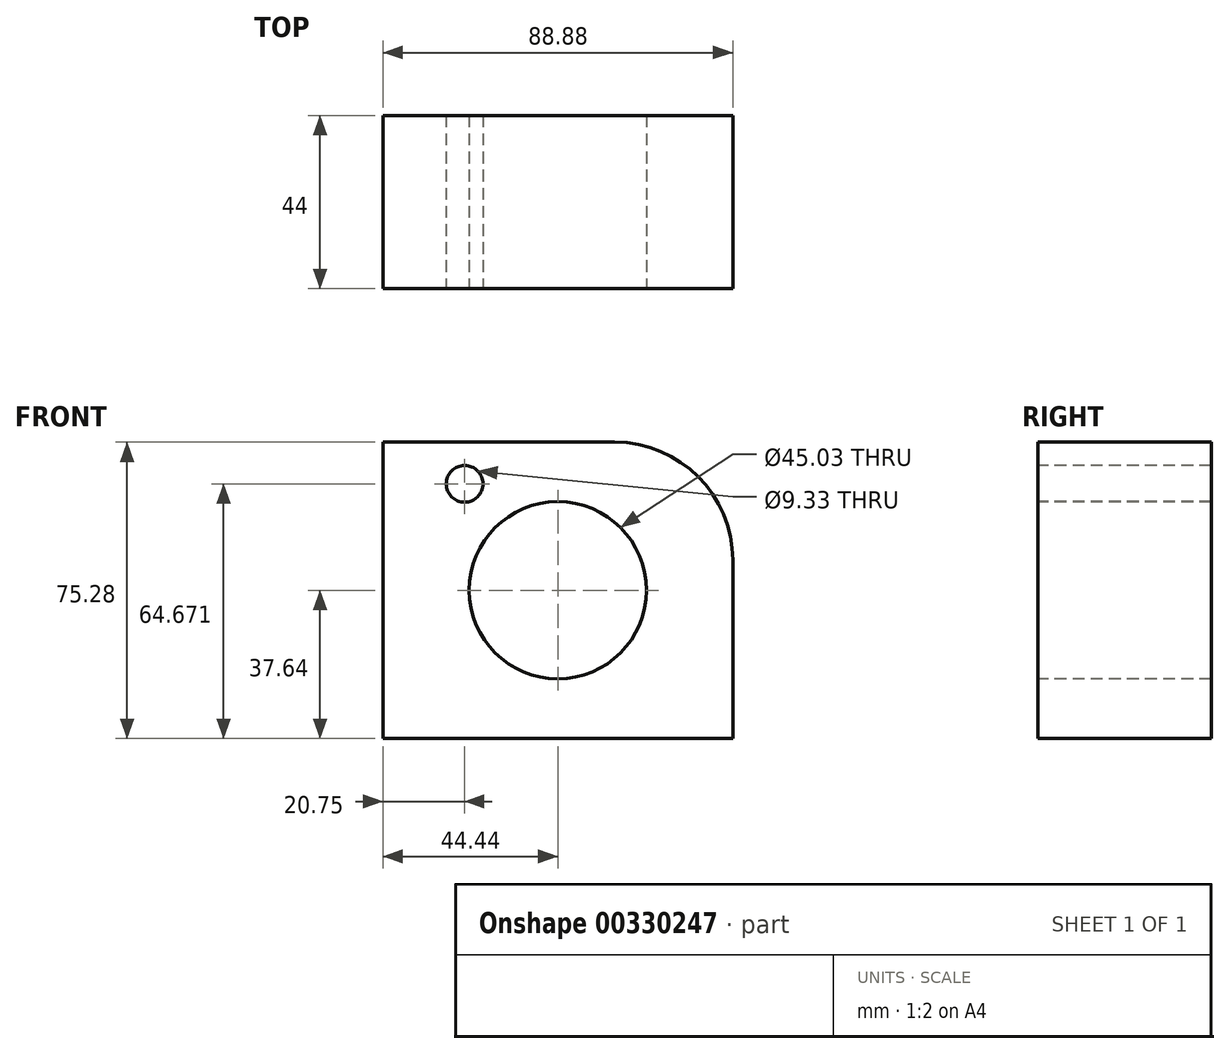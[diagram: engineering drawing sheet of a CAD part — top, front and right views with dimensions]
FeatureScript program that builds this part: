
annotation { "Feature Type Name" : "Feature", "Feature Type Description" : "" }
export const myFeature = defineFeature(function(context is Context, id is Id, definition is map)
    precondition{}
    {
        {
            var Q0;
            Q0=qCreatedBy(makeId("Front.planeOp"),FACE);
            var sketch = newSketch(context, id + "F0", { "sketchPlane" : qUnion([Q0])});
            skLineSegment(sketch, "E0.bottom", {"start": v(-44.44, 37.64) * mm, "end": v(44.44, 37.64) * mm});
            skLineSegment(sketch, "E0.top", {"start": v(-44.44, -37.64) * mm, "end": v(44.44, -37.64) * mm});
            skLineSegment(sketch, "E0.left", {"start": v(-44.44, 37.64) * mm, "end": v(-44.44, -37.64) * mm});
            skLineSegment(sketch, "E0.right", {"start": v(44.44, 37.64) * mm, "end": v(44.44, -37.64) * mm});
            skPoint(sketch, "E0.middle", {"position": v(0, 0) * mm});
            skSolve(sketch);
        }
        {
            var Q0;
            Q0=makeQuery(id+"F0.imprint","IMPRINT",FACE,{"disambiguationData":[TD([[makeQuery(id+"F0.imprint","IMPRINT",EDGE,{"derivedFrom":sQuery(id+"F0.wireOp",EDGE,"E0.bottom")}),-1.0]])]});
            extrude(context, id + "F1", {"entities" : qUnion([Q0]), "depth" : 44 * mm});
        }
        {
            var Q0;
            Q0=makeQuery(id+"F1.opExtrude","CAP_FACE",FACE,{"disambiguationData":[OSD([sQuery(id+"F0.wireOp",EDGE,"E0.bottom"),sQuery(id+"F0.wireOp",EDGE,"E0.top"),sQuery(id+"F0.wireOp",EDGE,"E0.left"),sQuery(id+"F0.wireOp",EDGE,"E0.right")])],"isStart":false});
            var sketch = newSketch(context, id + "F2", { "sketchPlane" : qUnion([Q0])});
            skCircle(sketch, "E1", {"center": v(0, 0) * mm, "radius": 22.51 * mm});
            skSolve(sketch);
        }
        {
            var Q0;
            Q0=makeQuery(id+"F2.imprint","IMPRINT",FACE,{"disambiguationData":[TD([[makeQuery(id+"F2.imprint","IMPRINT",EDGE,{"derivedFrom":sQuery(id+"F2.wireOp",EDGE,"E1")}),1.0]])]});
            extrude(context, id + "F3", {"entities" : qUnion([Q0]), "operationType" : NewBodyOperationType.REMOVE, "endBound" : BoundingType.THROUGH_ALL, "oppositeDirection" : true, "depth" : 25 * mm});
        }
        {
            var Q0;
            Q0=makeQuery(id+"F1.opExtrude","CAP_FACE",FACE,{"disambiguationData":[OSD([sQuery(id+"F0.wireOp",EDGE,"E0.bottom"),sQuery(id+"F0.wireOp",EDGE,"E0.top"),sQuery(id+"F0.wireOp",EDGE,"E0.left"),sQuery(id+"F0.wireOp",EDGE,"E0.right")])],"isStart":false});
            var sketch = newSketch(context, id + "F4", { "sketchPlane" : qUnion([Q0])});
            skCircle(sketch, "E2", {"center": v(-23.69, 27.03) * mm, "radius": 4.66 * mm});
            skSolve(sketch);
        }
        {
            var Q0;
            Q0=makeQuery(id+"F4.imprint","IMPRINT",FACE,{"disambiguationData":[TD([[makeQuery(id+"F4.imprint","IMPRINT",EDGE,{"derivedFrom":sQuery(id+"F4.wireOp",EDGE,"E2")}),1.0]])]});
            extrude(context, id + "F5", {"entities" : qUnion([Q0]), "operationType" : NewBodyOperationType.REMOVE, "endBound" : BoundingType.THROUGH_ALL, "oppositeDirection" : true, "depth" : 25 * mm});
        }
        {
            var Q0;
            Q0=makeQuery(id+"F1.opExtrude","SWEPT_EDGE",EDGE,{"disambiguationData":[OSD([sQuery(id+"F0.wireOp",EDGE,"E0.bottom"),sQuery(id+"F0.wireOp",EDGE,"E0.right")])]});
            fillet(context, id + "F6", {"entities" : qUnion([Q0]), "radius" : 30 * mm, "tangentPropagation" : true, "allowEdgeOverflow" : false});
        }
    });
